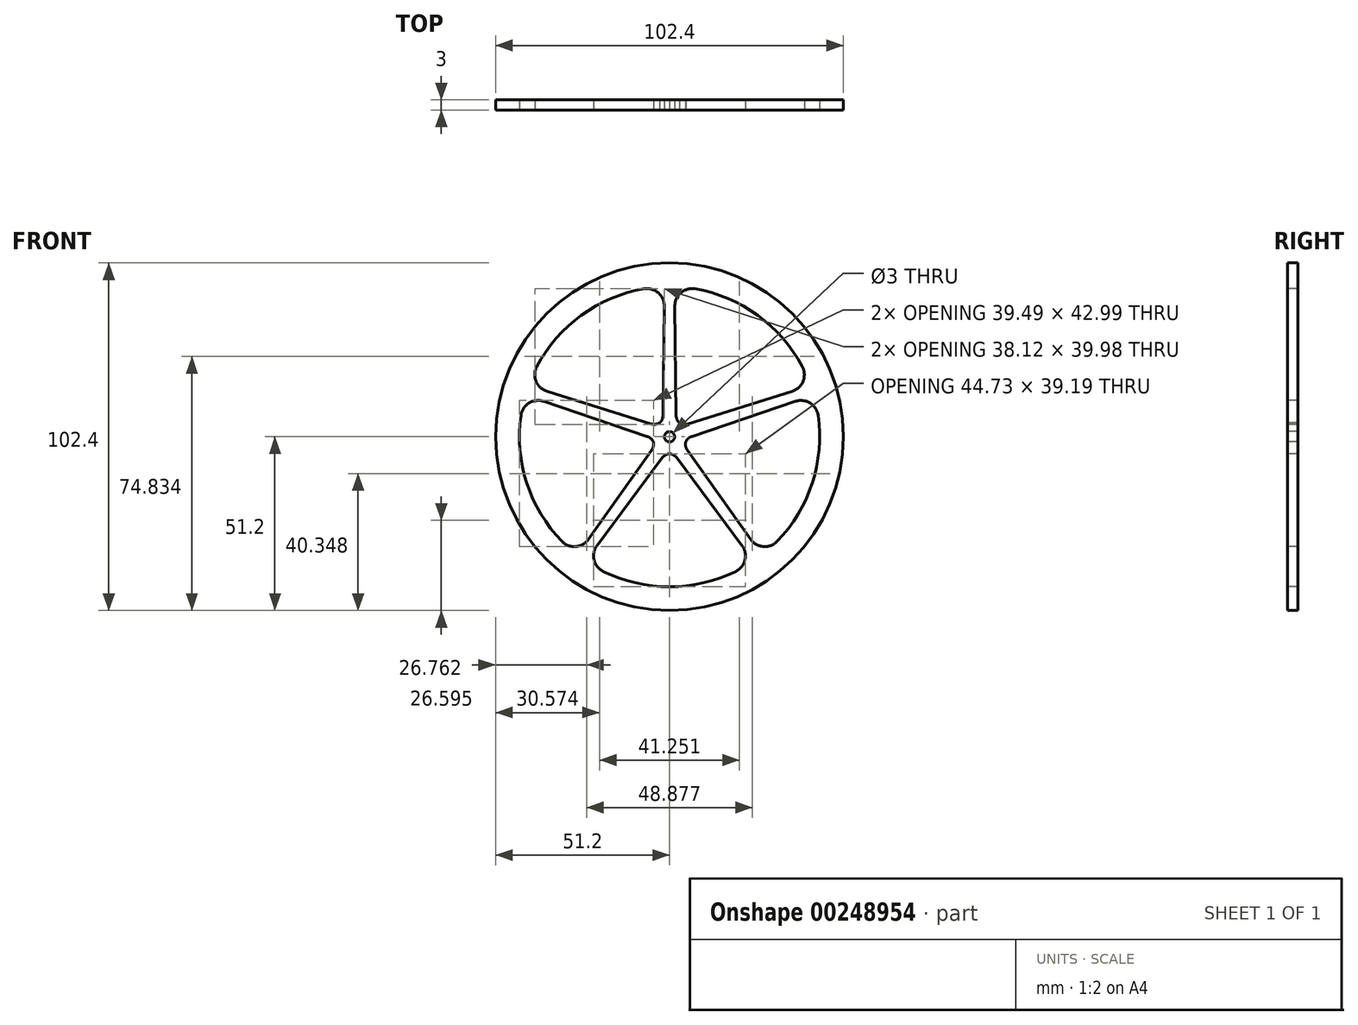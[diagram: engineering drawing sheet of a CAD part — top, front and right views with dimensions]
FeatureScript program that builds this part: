
annotation { "Feature Type Name" : "Feature", "Feature Type Description" : "" }
export const myFeature = defineFeature(function(context is Context, id is Id, definition is map)
    precondition{}
    {
        {
            var Q0;
            Q0=qCreatedBy(makeId("Front.planeOp"),FACE);
            var sketch = newSketch(context, id + "F0", { "sketchPlane" : qUnion([Q0])});
            skCircle(sketch, "E0", {"center": v(0, 0) * mm, "radius": 51.2 * mm});
            skCircle(sketch, "E1", {"center": v(0, 0) * mm, "radius": 1.5 * mm});
            skCircle(sketch, "E2", {"center": v(0, 0) * mm, "radius": 5 * mm});
            skCircle(sketch, "E3", {"center": v(0, 0) * mm, "radius": 44.2 * mm});
            skLineSegment(sketch, "E4", {"start": v(0, 0) * mm, "end": v(0, 1.5) * mm});
            skLineSegment(sketch, "E5", {"start": v(-1.96, 4.6) * mm, "end": v(-1.5, 44.17) * mm});
            skLineSegment(sketch, "E6.MirrorCS", {"start": v(1.96, 4.6) * mm, "end": v(1.5, 44.17) * mm});
            skLineSegment(sketch, "E7.1.0", {"start": v(-3.77, 3.29) * mm, "end": v(-41.55, 15.08) * mm});
            skLineSegment(sketch, "E7.1.1", {"start": v(-4.98, -0.44) * mm, "end": v(-42.48, 12.22) * mm});
            skLineSegment(sketch, "E7.2.0", {"start": v(-4.29, -2.57) * mm, "end": v(-27.18, -34.86) * mm});
            skLineSegment(sketch, "E7.2.1", {"start": v(-1.12, -4.87) * mm, "end": v(-24.75, -36.62) * mm});
            skLineSegment(sketch, "E7.3.0", {"start": v(1.12, -4.87) * mm, "end": v(24.75, -36.62) * mm});
            skLineSegment(sketch, "E7.3.1", {"start": v(4.29, -2.57) * mm, "end": v(27.18, -34.86) * mm});
            skLineSegment(sketch, "E7.4.0", {"start": v(4.98, -0.44) * mm, "end": v(42.48, 12.22) * mm});
            skLineSegment(sketch, "E7.4.1", {"start": v(3.77, 3.29) * mm, "end": v(41.55, 15.08) * mm});
            skSolve(sketch);
        }
        {
            var Q0;
            Q0=makeQuery(id+"F0.imprint","IMPRINT",FACE,{"disambiguationData":[TD([[makeQuery(id+"F0.imprint","IMPRINT",EDGE,{"derivedFrom":sQuery(id+"F0.wireOp",EDGE,"E0")}),1.0]])]});
            var Q1;
            {var subQ0=sQuery(id+"F0.wireOp",EDGE,"E7.2.0");Q1=makeQuery(id+"F0.imprint","IMPRINT",FACE,{"disambiguationData":[TD([[makeQuery(id+"F0.imprint","IMPRINT",EDGE,{"derivedFrom":subQ0}),1.0]])]});}
            var Q2;
            {var subQ0=sQuery(id+"F0.wireOp",EDGE,"E7.1.0");Q2=makeQuery(id+"F0.imprint","IMPRINT",FACE,{"disambiguationData":[TD([[makeQuery(id+"F0.imprint","IMPRINT",EDGE,{"derivedFrom":subQ0}),1.0]])]});}
            var Q3;
            {var subQ0=sQuery(id+"F0.wireOp",EDGE,"E5");Q3=makeQuery(id+"F0.imprint","IMPRINT",FACE,{"disambiguationData":[TD([[makeQuery(id+"F0.imprint","IMPRINT",EDGE,{"derivedFrom":subQ0}),-1.0]])]});}
            var Q4;
            {var subQ0=sQuery(id+"F0.wireOp",EDGE,"E7.4.0");Q4=makeQuery(id+"F0.imprint","IMPRINT",FACE,{"disambiguationData":[TD([[makeQuery(id+"F0.imprint","IMPRINT",EDGE,{"derivedFrom":subQ0}),1.0]])]});}
            var Q5;
            {var subQ0=sQuery(id+"F0.wireOp",EDGE,"E7.3.0");Q5=makeQuery(id+"F0.imprint","IMPRINT",FACE,{"disambiguationData":[TD([[makeQuery(id+"F0.imprint","IMPRINT",EDGE,{"derivedFrom":subQ0}),1.0]])]});}
            var Q6;
            Q6=makeQuery(id+"F0.imprint","IMPRINT",FACE,{"disambiguationData":[TD([[makeQuery(id+"F0.imprint","IMPRINT",EDGE,{"derivedFrom":sQuery(id+"F0.wireOp",EDGE,"E1")}),-1.0]])]});
            var Q7;
            Q7=sQuery(id+"F0.wireOp",EDGE,"E1");
            var Q8;
            Q8=sQuery(id+"F0.wireOp",EDGE,"E0");
            extrude(context, id + "F1", {"entities" : qUnion([Q0, Q1, Q2, Q3, Q4, Q5, Q6]), "surfaceEntities" : qUnion([Q7, Q8]), "endBound" : BoundingType.SYMMETRIC, "oppositeDirection" : true, "depth" : 3 * mm});
        }
        {
            var Q0;
            Q0=makeQuery(id+"F1.opExtrude","SWEPT_EDGE",EDGE,{"disambiguationData":[OSD([sQuery(id+"F0.wireOp",EDGE,"E2"),sQuery(id+"F0.wireOp",EDGE,"E6.MirrorCS")])]});
            var Q1;
            Q1=makeQuery(id+"F1.opExtrude","SWEPT_EDGE",EDGE,{"disambiguationData":[OSD([sQuery(id+"F0.wireOp",EDGE,"E2"),sQuery(id+"F0.wireOp",EDGE,"E7.4.1")])]});
            var Q2;
            Q2=makeQuery(id+"F1.opExtrude","SWEPT_EDGE",EDGE,{"disambiguationData":[OSD([sQuery(id+"F0.wireOp",EDGE,"E2"),sQuery(id+"F0.wireOp",EDGE,"E7.1.0")])]});
            var Q3;
            Q3=makeQuery(id+"F1.opExtrude","SWEPT_EDGE",EDGE,{"disambiguationData":[OSD([sQuery(id+"F0.wireOp",EDGE,"E2"),sQuery(id+"F0.wireOp",EDGE,"E5")])]});
            var Q4;
            Q4=makeQuery(id+"F1.opExtrude","SWEPT_EDGE",EDGE,{"disambiguationData":[OSD([sQuery(id+"F0.wireOp",EDGE,"E2"),sQuery(id+"F0.wireOp",EDGE,"E7.1.1")])]});
            var Q5;
            Q5=makeQuery(id+"F1.opExtrude","SWEPT_EDGE",EDGE,{"disambiguationData":[OSD([sQuery(id+"F0.wireOp",EDGE,"E2"),sQuery(id+"F0.wireOp",EDGE,"E7.2.0")])]});
            var Q6;
            Q6=makeQuery(id+"F1.opExtrude","SWEPT_EDGE",EDGE,{"disambiguationData":[OSD([sQuery(id+"F0.wireOp",EDGE,"E2"),sQuery(id+"F0.wireOp",EDGE,"E7.4.0")])]});
            var Q7;
            Q7=makeQuery(id+"F1.opExtrude","SWEPT_EDGE",EDGE,{"disambiguationData":[OSD([sQuery(id+"F0.wireOp",EDGE,"E2"),sQuery(id+"F0.wireOp",EDGE,"E7.3.1")])]});
            var Q8;
            Q8=makeQuery(id+"F1.opExtrude","SWEPT_EDGE",EDGE,{"disambiguationData":[OSD([sQuery(id+"F0.wireOp",EDGE,"E2"),sQuery(id+"F0.wireOp",EDGE,"E7.2.1")])]});
            var Q9;
            Q9=makeQuery(id+"F1.opExtrude","SWEPT_EDGE",EDGE,{"disambiguationData":[OSD([sQuery(id+"F0.wireOp",EDGE,"E2"),sQuery(id+"F0.wireOp",EDGE,"E7.3.0")])]});
            fillet(context, id + "F2", {"entities" : qUnion([Q0, Q1, Q2, Q3, Q4, Q5, Q6, Q7, Q8, Q9]), "radius" : 3 * mm, "tangentPropagation" : true, "allowEdgeOverflow" : false});
        }
        {
            var Q0;
            Q0=makeQuery(id+"F1.opExtrude","SWEPT_EDGE",EDGE,{"disambiguationData":[OSD([sQuery(id+"F0.wireOp",EDGE,"E3"),sQuery(id+"F0.wireOp",EDGE,"E7.1.1")])]});
            var Q1;
            Q1=makeQuery(id+"F1.opExtrude","SWEPT_EDGE",EDGE,{"disambiguationData":[OSD([sQuery(id+"F0.wireOp",EDGE,"E3"),sQuery(id+"F0.wireOp",EDGE,"E7.4.0")])]});
            var Q2;
            Q2=makeQuery(id+"F1.opExtrude","SWEPT_EDGE",EDGE,{"disambiguationData":[OSD([sQuery(id+"F0.wireOp",EDGE,"E3"),sQuery(id+"F0.wireOp",EDGE,"E5")])]});
            var Q3;
            Q3=makeQuery(id+"F1.opExtrude","SWEPT_EDGE",EDGE,{"disambiguationData":[OSD([sQuery(id+"F0.wireOp",EDGE,"E3"),sQuery(id+"F0.wireOp",EDGE,"E7.3.0")])]});
            var Q4;
            Q4=makeQuery(id+"F1.opExtrude","SWEPT_EDGE",EDGE,{"disambiguationData":[OSD([sQuery(id+"F0.wireOp",EDGE,"E3"),sQuery(id+"F0.wireOp",EDGE,"E7.3.1")])]});
            var Q5;
            Q5=makeQuery(id+"F1.opExtrude","SWEPT_EDGE",EDGE,{"disambiguationData":[OSD([sQuery(id+"F0.wireOp",EDGE,"E3"),sQuery(id+"F0.wireOp",EDGE,"E7.4.1")])]});
            var Q6;
            Q6=makeQuery(id+"F1.opExtrude","SWEPT_EDGE",EDGE,{"disambiguationData":[OSD([sQuery(id+"F0.wireOp",EDGE,"E3"),sQuery(id+"F0.wireOp",EDGE,"E6.MirrorCS")])]});
            var Q7;
            Q7=makeQuery(id+"F1.opExtrude","SWEPT_EDGE",EDGE,{"disambiguationData":[OSD([sQuery(id+"F0.wireOp",EDGE,"E3"),sQuery(id+"F0.wireOp",EDGE,"E7.1.0")])]});
            var Q8;
            Q8=makeQuery(id+"F1.opExtrude","SWEPT_EDGE",EDGE,{"disambiguationData":[OSD([sQuery(id+"F0.wireOp",EDGE,"E3"),sQuery(id+"F0.wireOp",EDGE,"E7.2.0")])]});
            var Q9;
            Q9=makeQuery(id+"F1.opExtrude","SWEPT_EDGE",EDGE,{"disambiguationData":[OSD([sQuery(id+"F0.wireOp",EDGE,"E3"),sQuery(id+"F0.wireOp",EDGE,"E7.2.1")])]});
            fillet(context, id + "F3", {"entities" : qUnion([Q0, Q1, Q2, Q3, Q4, Q5, Q6, Q7, Q8, Q9]), "radius" : 5.08 * mm, "tangentPropagation" : true, "allowEdgeOverflow" : false});
        }
    });
